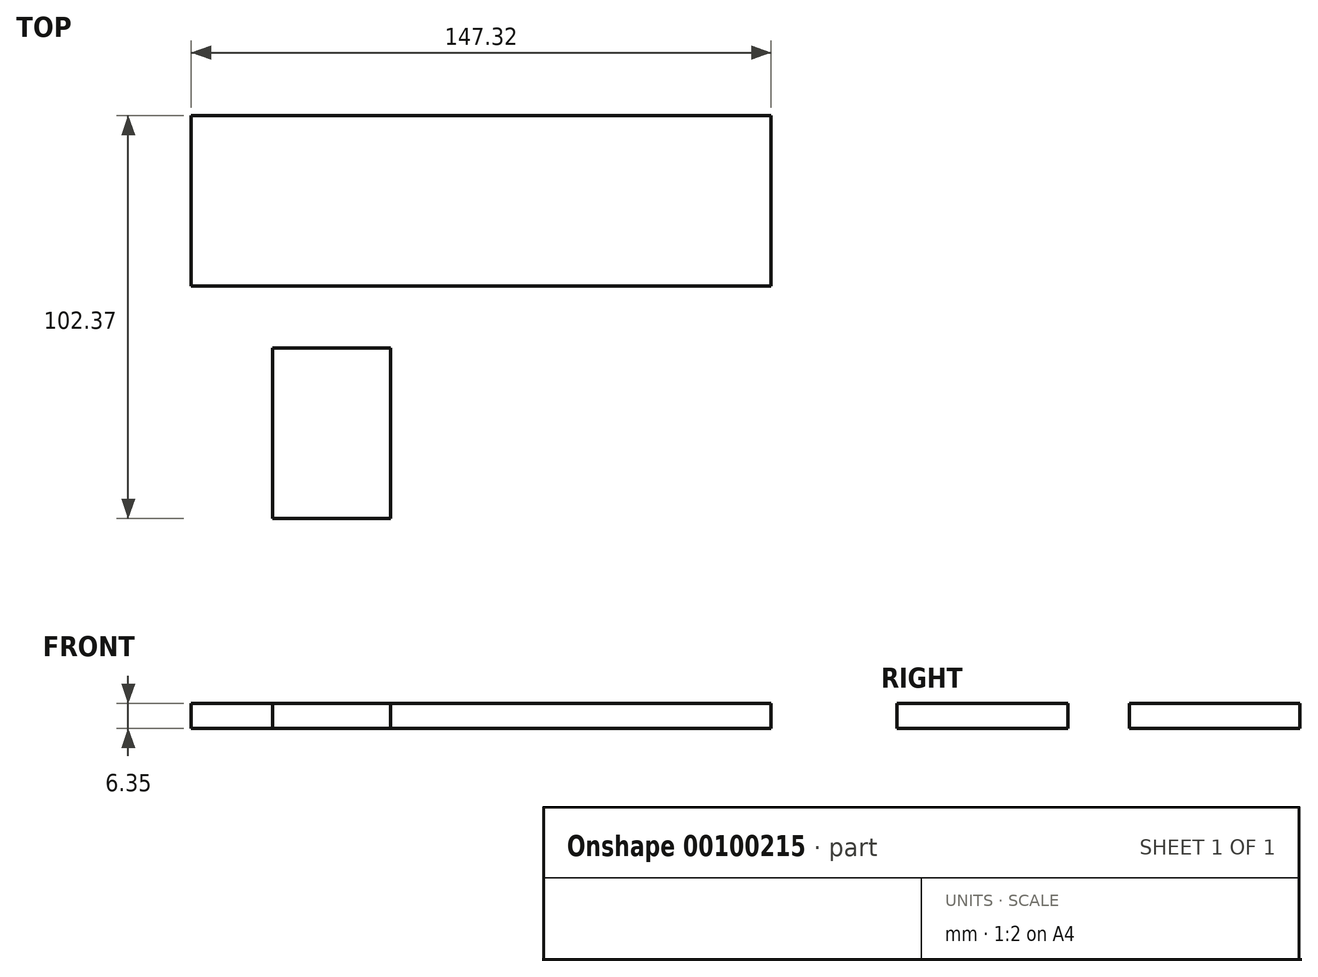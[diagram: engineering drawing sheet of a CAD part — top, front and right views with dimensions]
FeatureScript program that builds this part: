
annotation { "Feature Type Name" : "Feature", "Feature Type Description" : "" }
export const myFeature = defineFeature(function(context is Context, id is Id, definition is map)
    precondition{}
    {
        {
            var Q0;
            Q0=qCreatedBy(makeId("Top.planeOp"),FACE);
            var sketch = newSketch(context, id + "F0", { "sketchPlane" : qUnion([Q0])});
            skLineSegment(sketch, "E0.bottom", {"start": v(-77.2, 43.35) * mm, "end": v(70.13, 43.35) * mm});
            skLineSegment(sketch, "E0.top", {"start": v(-77.2, 0) * mm, "end": v(70.13, 0) * mm});
            skLineSegment(sketch, "E0.left", {"start": v(-77.2, 43.35) * mm, "end": v(-77.2, 0) * mm});
            skLineSegment(sketch, "E0.right", {"start": v(70.13, 43.35) * mm, "end": v(70.13, 0) * mm});
            skSolve(sketch);
        }
        {
            var Q0;
            Q0=qCreatedBy(makeId("Top.planeOp"),FACE);
            var sketch = newSketch(context, id + "F1", { "sketchPlane" : qUnion([Q0])});
            skLineSegment(sketch, "E1.bottom", {"start": v(-56.57, -15.67) * mm, "end": v(-26.57, -15.67) * mm});
            skLineSegment(sketch, "E1.top", {"start": v(-56.57, -59.02) * mm, "end": v(-26.57, -59.02) * mm});
            skLineSegment(sketch, "E1.left", {"start": v(-56.57, -15.67) * mm, "end": v(-56.57, -59.02) * mm});
            skLineSegment(sketch, "E1.right", {"start": v(-26.57, -15.67) * mm, "end": v(-26.57, -59.02) * mm});
            skSolve(sketch);
        }
        {
            var Q0;
            Q0=makeQuery(id+"F0.imprint","IMPRINT",FACE,{"disambiguationData":[TD([[makeQuery(id+"F0.imprint","IMPRINT",EDGE,{"derivedFrom":sQuery(id+"F0.wireOp",EDGE,"E0.bottom")}),-1.0]])]});
            extrude(context, id + "F2", {"entities" : qUnion([Q0]), "depth" : 6.35 * mm});
        }
        {
            var Q0;
            Q0=makeQuery(id+"F1.imprint","IMPRINT",FACE,{"disambiguationData":[TD([[makeQuery(id+"F1.imprint","IMPRINT",EDGE,{"derivedFrom":sQuery(id+"F1.wireOp",EDGE,"E1.bottom")}),-1.0]])]});
            extrude(context, id + "F3", {"entities" : qUnion([Q0]), "depth" : 6.35 * mm});
        }
    });
